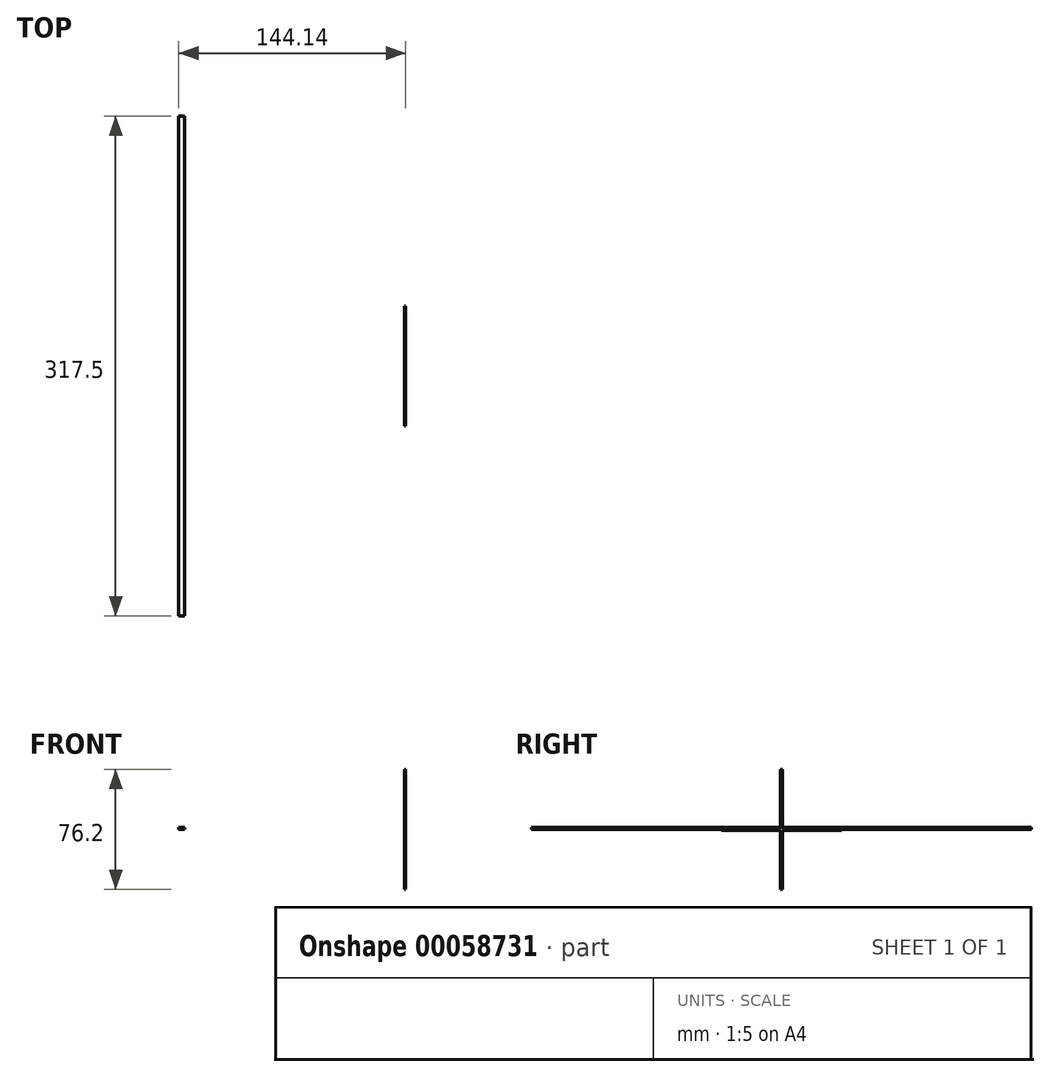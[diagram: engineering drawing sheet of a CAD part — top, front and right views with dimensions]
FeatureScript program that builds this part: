
annotation { "Feature Type Name" : "Feature", "Feature Type Description" : "" }
export const myFeature = defineFeature(function(context is Context, id is Id, definition is map)
    precondition{}
    {
        {
            var Q0;
            Q0=qCreatedBy(makeId("Top.planeOp"),FACE);
            var sketch = newSketch(context, id + "F0", { "sketchPlane" : qUnion([Q0])});
            skLineSegment(sketch, "E0.rect.bottom", {"start": v(-139.7, -158.75) * mm, "end": v(-143.5, -158.75) * mm});
            skLineSegment(sketch, "E0.rect.top", {"start": v(-139.7, 158.75) * mm, "end": v(-143.5, 158.75) * mm});
            skLineSegment(sketch, "E0.rect.left", {"start": v(-139.7, -158.75) * mm, "end": v(-139.7, 158.75) * mm});
            skLineSegment(sketch, "E0.rect.right", {"start": v(-143.5, -158.75) * mm, "end": v(-143.5, 158.75) * mm});
            skPoint(sketch, "E0.rect.middle", {"position": v(-141.6, 0) * mm});
            skSolve(sketch);
        }
        {
            var Q0;
            Q0=makeQuery(id+"F0.imprint","IMPRINT",FACE,{"disambiguationData":[TD([[makeQuery(id+"F0.imprint","IMPRINT",EDGE,{"derivedFrom":sQuery(id+"F0.wireOp",EDGE,"E0.rect.bottom")}),-1.0]])]});
            extrude(context, id + "F1", {"entities" : qUnion([Q0]), "depth" : 1.27 * mm});
        }
        {
            var Q0;
            Q0=qCreatedBy(makeId("Right.planeOp"),FACE);
            var sketch = newSketch(context, id + "F2", { "sketchPlane" : qUnion([Q0])});
            skLineSegment(sketch, "E1.rect.bottom", {"start": v(0.63, -38.1) * mm, "end": v(-0.64, -38.1) * mm});
            skLineSegment(sketch, "E1.rect.top", {"start": v(0.64, 38.1) * mm, "end": v(-0.64, 38.1) * mm});
            skLineSegment(sketch, "E1.rect.left", {"start": v(0.63, -38.1) * mm, "end": v(0.64, 38.1) * mm});
            skLineSegment(sketch, "E1.rect.right", {"start": v(-0.64, -38.1) * mm, "end": v(-0.64, 38.1) * mm});
            skPoint(sketch, "E1.rect.middle", {"position": v(0, 0) * mm});
            skLineSegment(sketch, "E2.rect.bottom", {"start": v(-38.1, 0.64) * mm, "end": v(38.1, 0.64) * mm});
            skLineSegment(sketch, "E2.rect.top", {"start": v(-38.1, -0.64) * mm, "end": v(38.1, -0.64) * mm});
            skLineSegment(sketch, "E2.rect.left", {"start": v(-38.1, 0.64) * mm, "end": v(-38.1, -0.64) * mm});
            skLineSegment(sketch, "E2.rect.right", {"start": v(38.1, 0.64) * mm, "end": v(38.1, -0.64) * mm});
            skSolve(sketch);
        }
        {
            var Q0;
            {var subQ5=sQuery(id+"F2.wireOp",EDGE,"E2.rect.right");Q0=makeQuery(id+"F2.imprint","IMPRINT",FACE,{"disambiguationData":[TD([[makeQuery(id+"F2.imprint","IMPRINT",EDGE,{"derivedFrom":subQ5}),-1.0]])]});}
            var Q1;
            {var subQ5=sQuery(id+"F2.wireOp",EDGE,"E2.rect.left");Q1=makeQuery(id+"F2.imprint","IMPRINT",FACE,{"disambiguationData":[TD([[makeQuery(id+"F2.imprint","IMPRINT",EDGE,{"derivedFrom":subQ5}),1.0]])]});}
            var Q2;
            {var subQ0=sQuery(id+"F2.wireOp",EDGE,"E1.rect.top");Q2=makeQuery(id+"F2.imprint","IMPRINT",FACE,{"disambiguationData":[TD([[makeQuery(id+"F2.imprint","IMPRINT",EDGE,{"derivedFrom":subQ0}),1.0]])]});}
            var Q3;
            {var subQ0=sQuery(id+"F2.wireOp",EDGE,"E1.rect.bottom");Q3=makeQuery(id+"F2.imprint","IMPRINT",FACE,{"disambiguationData":[TD([[makeQuery(id+"F2.imprint","IMPRINT",EDGE,{"derivedFrom":subQ0}),-1.0]])]});}
            var Q4;
            {var subQ0=sQuery(id+"F2.wireOp",EDGE,"E2.rect.top");var subQ1=sQuery(id+"F2.wireOp",EDGE,"E1.rect.left");var subQ2=makeQuery(id+"F2.imprint","INTERSECT",VERTEX,{"derivedFrom":[subQ1,subQ0]});Q4=makeQuery(id+"F2.imprint","IMPRINT",FACE,{"disambiguationData":[TD([[makeQuery(id+"F2.imprint","IMPRINT",EDGE,{"disambiguationData":[TD([[subQ2,-1.0]])],"derivedFrom":subQ1}),1.0]])]});}
            extrude(context, id + "F3", {"entities" : qUnion([Q0, Q1, Q2, Q3, Q4]), "depth" : 0.64 * mm});
        }
    });
